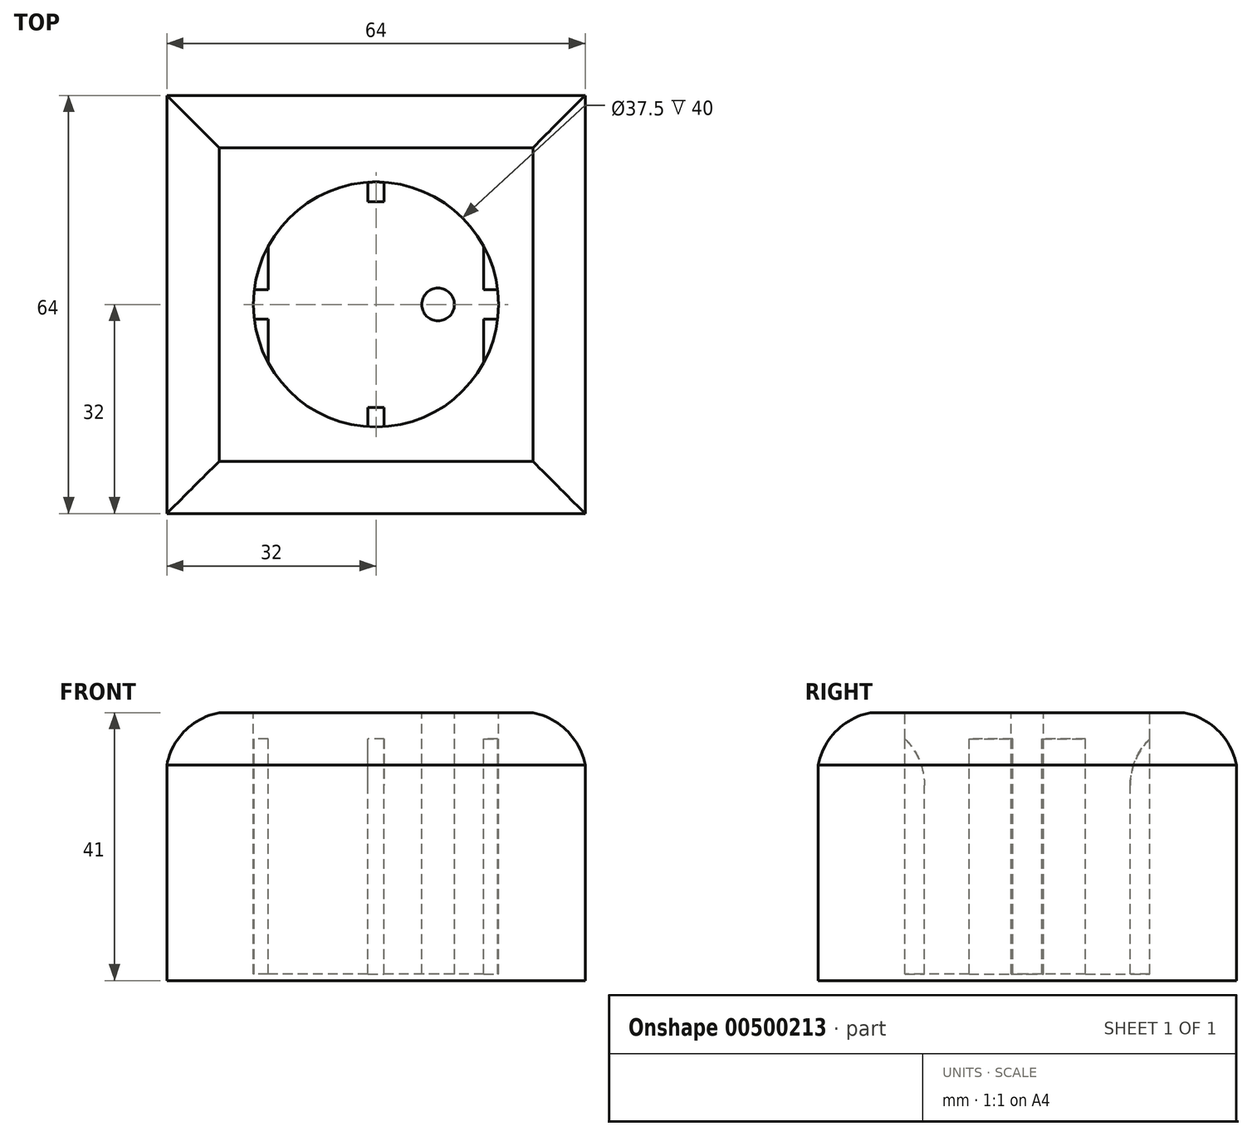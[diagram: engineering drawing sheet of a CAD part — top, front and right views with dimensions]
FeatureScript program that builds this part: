
annotation { "Feature Type Name" : "Feature", "Feature Type Description" : "" }
export const myFeature = defineFeature(function(context is Context, id is Id, definition is map)
    precondition{}
    {
        {
            var Q0;
            Q0=qCreatedBy(makeId("Front.planeOp"),FACE);
            var sketch = newSketch(context, id + "F0", { "sketchPlane" : qUnion([Q0])});
            skLineSegment(sketch, "E0.bottom", {"start": v(-24, 41) * mm, "end": v(24, 41) * mm});
            skLineSegment(sketch, "E0.top", {"start": v(-32, 0) * mm, "end": v(32, 0) * mm});
            skLineSegment(sketch, "E0.left", {"start": v(-32, 33) * mm, "end": v(-32, 0) * mm});
            skLineSegment(sketch, "E0.right", {"start": v(32, 33) * mm, "end": v(32, 0) * mm});
            skPoint(sketch, "E1.visualSharp", {"position": v(-32, 41) * mm});
            skArc(sketch, "E1.filletArc", {"start": v(-24, 41) * mm, "mid": v(-29.24, 38.24) * mm, "end": v(-32, 33) * mm});
            skPoint(sketch, "E2.visualSharp", {"position": v(32, 41) * mm});
            skArc(sketch, "E2.filletArc", {"start": v(32, 33) * mm, "mid": v(29.24, 38.24) * mm, "end": v(24, 41) * mm});
            skLineSegment(sketch, "E3", {"start": v(0, 0) * mm, "end": v(0, 41) * mm, "construction": true});
            skSolve(sketch);
        }
        {
            var Q0;
            Q0 = qSketchRegion(id + "F0", true);
            extrude(context, id + "F1", {"entities" : qUnion([Q0]), "depth" : 64 * mm, "offsetDistance" : 25 * mm, "symmetric" : true});
        }
        {
            var Q0;
            Q0=makeQuery(id+"F1.opExtrude","SWEPT_BODY",BODY,{"disambiguationData":[OSD([sQuery(id+"F0.wireOp",EDGE,"E0.bottom"),sQuery(id+"F0.wireOp",EDGE,"E0.top"),sQuery(id+"F0.wireOp",EDGE,"E0.left"),sQuery(id+"F0.wireOp",EDGE,"E0.right"),sQuery(id+"F0.wireOp",EDGE,"E1.filletArc"),sQuery(id+"F0.wireOp",EDGE,"E2.filletArc")])]});
            var Q1;
            Q1=sQuery(id+"F0.wireOp",EDGE,"E3");
            transform(context, id + "F2", {"entities" : qUnion([Q0]), "transformType" : TransformType.ROTATION, "transformAxis" : qUnion([Q1]), "angle" : 90 * degree, "makeCopy" : false});
        }
        {
            var Q0;
            Q0 = qSketchRegion(id + "F0", true);
            extrude(context, id + "F3", {"entities" : qUnion([Q0]), "operationType" : NewBodyOperationType.INTERSECT, "depth" : 64 * mm, "offsetDistance" : 25 * mm, "symmetric" : true});
        }
        {
            var Q0;
            Q0=makeQuery(id+"F1.opExtrude","SWEPT_FACE",FACE,{"disambiguationData":[OSD([sQuery(id+"F0.wireOp",EDGE,"E0.bottom")])]});
            var sketch = newSketch(context, id + "F4", { "sketchPlane" : qUnion([Q0])});
            skCircle(sketch, "E4", {"center": v(0, 0) * mm, "radius": 18.75 * mm});
            skCircle(sketch, "E5", {"center": v(-9.5, 0) * mm, "radius": 2.5 * mm});
            skLineSegment(sketch, "E6", {"start": v(-1.25, 18.7) * mm, "end": v(-1.25, 15.75) * mm});
            skLineSegment(sketch, "E7", {"start": v(-16.5, 8.9) * mm, "end": v(-16.5, 2.25) * mm});
            skLineSegment(sketch, "E8", {"start": v(-16.5, 2.25) * mm, "end": v(-18.61, 2.25) * mm});
            skLineSegment(sketch, "E9", {"start": v(-18.75, 0) * mm, "end": v(18.75, 0) * mm, "construction": true});
            skLineSegment(sketch, "E10", {"start": v(0, 18.75) * mm, "end": v(0, -18.75) * mm, "construction": true});
            skLineSegment(sketch, "E11.MirrorCS", {"start": v(-16.5, -2.25) * mm, "end": v(-18.61, -2.25) * mm});
            skLineSegment(sketch, "E12.MirrorCS", {"start": v(-16.5, -8.9) * mm, "end": v(-16.5, -2.25) * mm});
            skLineSegment(sketch, "E13.MirrorCS", {"start": v(-1.25, -18.7) * mm, "end": v(-1.25, -15.75) * mm});
            skCircle(sketch, "E14.MirrorC", {"center": v(9.5, 0) * mm, "radius": 2.5 * mm});
            skLineSegment(sketch, "E15.MirrorCS", {"start": v(1.25, -18.7) * mm, "end": v(1.25, -15.75) * mm});
            skLineSegment(sketch, "E16.MirrorCS", {"start": v(16.5, -8.9) * mm, "end": v(16.5, -2.25) * mm});
            skLineSegment(sketch, "E17.MirrorCS", {"start": v(16.5, -2.25) * mm, "end": v(18.61, -2.25) * mm});
            skLineSegment(sketch, "E18.MirrorCS", {"start": v(16.5, 2.25) * mm, "end": v(18.61, 2.25) * mm});
            skLineSegment(sketch, "E19.MirrorCS", {"start": v(16.5, 8.9) * mm, "end": v(16.5, 2.25) * mm});
            skLineSegment(sketch, "E20.MirrorCS", {"start": v(1.25, 18.7) * mm, "end": v(1.25, 15.75) * mm});
            skLineSegment(sketch, "E21", {"start": v(-1.25, 15.75) * mm, "end": v(1.25, 15.75) * mm});
            skLineSegment(sketch, "E22", {"start": v(-1.25, -15.75) * mm, "end": v(1.25, -15.75) * mm});
            skSolve(sketch);
        }
        {
            var Q0;
            Q0 = qSketchRegion(id + "F4", true);
            var Q1;
            Q1=makeQuery(id+"F4.imprint","IMPRINT",FACE,{"disambiguationData":[TD([[makeQuery(id+"F4.imprint","IMPRINT",EDGE,{"derivedFrom":sQuery(id+"F4.wireOp",EDGE,"E5")}),1.0]])]});
            var Q2;
            Q2=makeQuery(id+"F4.imprint","IMPRINT",FACE,{"disambiguationData":[TD([[makeQuery(id+"F4.imprint","IMPRINT",EDGE,{"derivedFrom":sQuery(id+"F4.wireOp",EDGE,"E14.MirrorC")}),-1.0]])]});
            extrude(context, id + "F5", {"entities" : qUnion([Q0, Q1, Q2]), "operationType" : NewBodyOperationType.REMOVE, "oppositeDirection" : true, "depth" : 21 * mm, "offsetDistance" : 25 * mm});
        }
        {
            var Q0;
            {var subQ0=sQuery(id+"F4.wireOp",EDGE,"E7");Q0=makeQuery(id+"F4.imprint","IMPRINT",FACE,{"disambiguationData":[TD([[makeQuery(id+"F4.imprint","IMPRINT",EDGE,{"derivedFrom":subQ0}),-1.0]])]});}
            var Q1;
            {var subQ0=sQuery(id+"F4.wireOp",EDGE,"E11.MirrorCS");Q1=makeQuery(id+"F4.imprint","IMPRINT",FACE,{"disambiguationData":[TD([[makeQuery(id+"F4.imprint","IMPRINT",EDGE,{"derivedFrom":subQ0}),1.0]])]});}
            var Q2;
            {var subQ0=sQuery(id+"F4.wireOp",EDGE,"E18.MirrorCS");Q2=makeQuery(id+"F4.imprint","IMPRINT",FACE,{"disambiguationData":[TD([[makeQuery(id+"F4.imprint","IMPRINT",EDGE,{"derivedFrom":subQ0}),1.0]])]});}
            var Q3;
            {var subQ0=sQuery(id+"F4.wireOp",EDGE,"E16.MirrorCS");Q3=makeQuery(id+"F4.imprint","IMPRINT",FACE,{"disambiguationData":[TD([[makeQuery(id+"F4.imprint","IMPRINT",EDGE,{"derivedFrom":subQ0}),-1.0]])]});}
            var Q4;
            {var subQ0=sQuery(id+"F4.wireOp",EDGE,"E6");Q4=makeQuery(id+"F4.imprint","IMPRINT",FACE,{"disambiguationData":[TD([[makeQuery(id+"F4.imprint","IMPRINT",EDGE,{"derivedFrom":subQ0}),1.0]])]});}
            var Q5;
            {var subQ0=sQuery(id+"F4.wireOp",EDGE,"E13.MirrorCS");Q5=makeQuery(id+"F4.imprint","IMPRINT",FACE,{"disambiguationData":[TD([[makeQuery(id+"F4.imprint","IMPRINT",EDGE,{"derivedFrom":subQ0}),-1.0]])]});}
            extrude(context, id + "F6", {"entities" : qUnion([Q0, Q1, Q2, Q3, Q4, Q5]), "operationType" : NewBodyOperationType.ADD, "oppositeDirection" : true, "depth" : 25 * mm, "offsetDistance" : 25 * mm, "hasSecondDirection" : true, "secondDirectionOppositeDirection" : true, "secondDirectionDepth" : 4 * mm});
        }
        {
            var Q0;
            Q0=makeQuery(id+"F6.opExtrude","CAP_EDGE",EDGE,{"disambiguationData":[OSD([sQuery(id+"F4.wireOp",EDGE,"E21")])],"isStart":true});
            var Q1;
            Q1=makeQuery(id+"F6.opExtrude","CAP_EDGE",EDGE,{"disambiguationData":[OSD([sQuery(id+"F4.wireOp",EDGE,"E22")])],"isStart":true});
            fillet(context, id + "F7", {"entities" : qUnion([Q0, Q1]), "radius" : 10 * mm, "tangentPropagation" : true, "allowEdgeOverflow" : false});
        }
        {
            var Q0;
            Q0=makeQuery(id+"F4.imprint","IMPRINT",FACE,{"disambiguationData":[TD([[makeQuery(id+"F4.imprint","IMPRINT",EDGE,{"derivedFrom":sQuery(id+"F4.wireOp",EDGE,"E5")}),1.0]])]});
            var Q1;
            Q1=makeQuery(id+"F4.imprint","IMPRINT",FACE,{"disambiguationData":[TD([[makeQuery(id+"F4.imprint","IMPRINT",EDGE,{"derivedFrom":sQuery(id+"F4.wireOp",EDGE,"E14.MirrorC")}),-1.0]])]});
            extrude(context, id + "F8", {"entities" : qUnion([Q0, Q1]), "operationType" : NewBodyOperationType.REMOVE, "oppositeDirection" : true, "depth" : 40 * mm, "offsetDistance" : 25 * mm});
        }
    });
